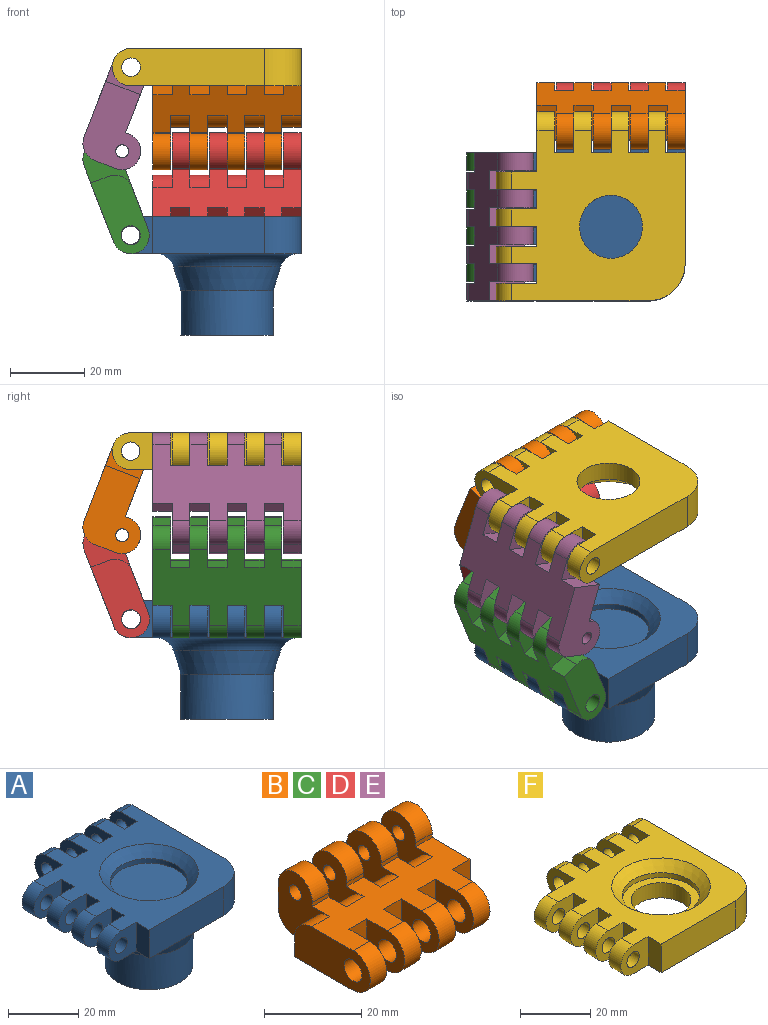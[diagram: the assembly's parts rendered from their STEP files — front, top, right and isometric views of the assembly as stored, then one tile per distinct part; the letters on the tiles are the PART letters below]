
ASSEMBLY  parts=6 mates=4
PART A: 59 faces, bbox 51.8x51.8x32 mm
  f0: cylinder r=8.5mm len=18.12mm, axis (0,0,-1), area 888.1mm2, adj f1,f52,f57
  f1: cylinder r=8.5mm len=17mm, axis (0,0,-1), area 16.5mm2, adj f0,f2
  f2: cylinder r=8.5mm len=17mm, axis (0,0,-1), area 16.5mm2, adj f1,f3
  f3: cylinder r=8.5mm len=17mm, axis (0,0,-1), area 16.5mm2, adj f2,f4
  f4: cylinder r=8.5mm len=17mm, axis (0,0,-1), area 16.5mm2, adj f3,f5
  f5: cylinder r=8.5mm len=7.56mm, axis (0,0,-1), area 1.2mm2, adj f4,f49
  f6: plane 16.2x10mm, normal (0,1,0), area 131.6mm2, adj f14,f15,f18,f38,f47
  f7: plane 11x10mm, normal (0,-1,0), area 79.6mm2, adj f14,f15,f25,f38,f47
  f8: plane 11x10mm, normal (0,1,0), area 79.6mm2, adj f14,f15,f25,f37,f46
  f9: plane 11x10mm, normal (0,-1,0), area 79.6mm2, adj f14,f15,f26,f37,f46
  f10: plane 11x10mm, normal (0,1,0), area 79.6mm2, adj f14,f15,f26,f36,f45
  f11: plane 11x10mm, normal (0,-1,0), area 79.6mm2, adj f14,f15,f27,f36,f45
  f12: plane 11x10mm, normal (0,1,0), area 79.6mm2, adj f14,f15,f27,f35,f44
  f13: plane 11x10mm, normal (0,-1,0), area 79.6mm2, adj f14,f15,f28,f35,f44
  f14: plane 46.83x46mm, normal (0,0,1), area 1209.2mm2, adj f6,f7,f8,f9,f10,f11,f12,f13
  f15: plane 46.83x46mm, normal (0,0,-1), area 664.4mm2, adj f6,f7,f8,f9,f10,f11,f12,f13
  f16: plane 11x10mm, normal (-1,0,0), area 80mm2, adj f14,f15,f24,f32,f40
  f17: plane 11x10mm, normal (1,0,0), area 80mm2, adj f14,f15,f24,f39,f43
  f18: plane 11x10mm, normal (-1,0,0), area 80mm2, adj f6,f14,f15,f39,f43
  f19: plane 41x10mm, normal (1,0,0), area 380mm2, adj f14,f15,f34,f42,f58
  f20: plane 11x10mm, normal (-1,0,0), area 80mm2, adj f14,f15,f30,f34,f42
  f21: plane 11x10mm, normal (1,0,0), area 80mm2, adj f14,f15,f30,f33,f41
  f22: plane 11x10mm, normal (-1,0,0), area 80mm2, adj f14,f15,f31,f33,f41
  f23: plane 11x10mm, normal (1,0,0), area 80mm2, adj f14,f15,f31,f32,f40
  f24: plane 10x5.2mm, normal (0,1,0), area 52mm2, adj f14,f15,f16,f17
  f25: plane 10x5.2mm, normal (-1,0,0), area 52mm2, adj f7,f8,f14,f15
  f26: plane 10x5.2mm, normal (-1,0,0), area 52mm2, adj f9,f10,f14,f15
  f27: plane 10x5.2mm, normal (-1,0,0), area 52mm2, adj f11,f12,f14,f15
  f28: plane 10x5.2mm, normal (-1,0,0), area 52mm2, adj f13,f14,f15,f29
  f29: plane 30x10mm, normal (0,-1,0), area 300mm2, adj f14,f15,f28,f58
  f30: plane 10x5.2mm, normal (0,1,0), area 52mm2, adj f14,f15,f20,f21
  f31: plane 10x5.2mm, normal (0,1,0), area 52mm2, adj f14,f15,f22,f23
  f32: cylinder r=2.5mm len=5mm, axis (-1,0,0), area 75.4mm2, adj f16,f23
  f33: cylinder r=2.5mm len=5mm, axis (-1,0,0), area 75.4mm2, adj f21,f22
  f34: cylinder r=2.5mm len=5mm, axis (-1,0,0), area 75.4mm2, adj f19,f20
  f35: cylinder r=2.5mm len=5mm, axis (0,-1,0), area 75.4mm2, adj f12,f13
  f36: cylinder r=2.5mm len=5mm, axis (0,-1,0), area 75.4mm2, adj f10,f11
  f37: cylinder r=2.5mm len=5mm, axis (0,-1,0), area 75.4mm2, adj f8,f9
  f38: cylinder r=2.5mm len=5mm, axis (0,-1,0), area 75.4mm2, adj f6,f7
  f39: cylinder r=2.5mm len=5mm, axis (-1,0,0), area 75.4mm2, adj f17,f18
  f40: cylinder r=5.08mm len=10mm, axis (-1,0,0), area 67.8mm2, adj f14,f15,f16,f23
  f41: cylinder r=5.08mm len=10mm, axis (-1,0,0), area 67.8mm2, adj f14,f15,f21,f22
  f42: cylinder r=5.08mm len=10mm, axis (-1,0,0), area 67.8mm2, adj f14,f15,f19,f20
  f43: cylinder r=5.08mm len=10mm, axis (-1,0,0), area 67.8mm2, adj f14,f15,f17,f18
  f44: cylinder r=5mm len=10mm, axis (0,-1,0), area 75.4mm2, adj f12,f13,f14,f15
  f45: cylinder r=5mm len=10mm, axis (0,-1,0), area 75.4mm2, adj f10,f11,f14,f15
  f46: cylinder r=5mm len=10mm, axis (0,-1,0), area 75.4mm2, adj f8,f9,f14,f15
  f47: cylinder r=5mm len=10mm, axis (0,-1,0), area 75.4mm2, adj f6,f7,f14,f15
  f48: cylinder r=12.5mm len=25mm, axis (0,0,1), area 942.5mm2, adj f49,f50
  f49: plane 25x25mm, normal (0,0,-1), area 228.2mm2, adj f5,f48,f53
  f50: cone r=12.5mm half-angle=16.7deg, axis (0,0,1), area 568.6mm2, adj f48,f51
  f51: torus R=19.22mm, axis (0,0,1), area 660.5mm2, adj f15,f50
  f52: plane 18.34x18.18mm, normal (0,0,-1), area 35.7mm2, adj f0,f53
  f53: cylinder r=9.7mm len=19.4mm, axis (0,0,1), area 116mm2, adj f49,f52
  f54: plane 22x22mm, normal (0,0,1), area 380.1mm2, adj f55
  f55: cylinder r=11mm len=22mm, axis (0,0,1), area 110.6mm2, adj f54,f56
  f56: cone r=11mm half-angle=45deg, axis (0,0,1), area 333.2mm2, adj f14,f55
  f57: plane 17x17mm, normal (0,0,-1), area 227mm2, adj f0
  f58: cylinder r=10mm len=10mm, axis (0,0,1), area 157.1mm2, adj f14,f15,f19,f29
PART B: 58 faces, bbox 40x32x16 mm
  f0: plane 5.2x5mm, normal (0,1,0), area 26mm2, adj f12,f31,f49,f57
  f1: plane 5.2x5mm, normal (0,1,0), area 26mm2, adj f12,f36,f43,f56
  f2: plane 5.2x5mm, normal (0,1,0), area 26mm2, adj f12,f37,f48,f54
  f3: plane 22x10mm, normal (-1,0,0), area 182.7mm2, adj f11,f12,f13,f22,f26,f55
  f4: plane 11x10mm, normal (1,0,0), area 78mm2, adj f11,f12,f14,f22,f26
  f5: plane 11x10mm, normal (-1,0,0), area 78mm2, adj f11,f12,f14,f21,f25
  f6: plane 11x10mm, normal (1,0,0), area 78mm2, adj f11,f12,f15,f21,f25
  f7: plane 11x10mm, normal (-1,0,0), area 78mm2, adj f11,f12,f15,f20,f24
  f8: plane 11x10mm, normal (1,0,0), area 78mm2, adj f11,f12,f16,f20,f24
  f9: plane 11x10mm, normal (-1,0,0), area 78mm2, adj f11,f12,f16,f19,f23
  f10: plane 11x10mm, normal (1,0,0), area 78mm2, adj f11,f12,f17,f19,f23
  f11: plane 40x17mm, normal (0,0,1), area 451.2mm2, adj f3,f4,f5,f6,f7,f8,f9,f10
  f12: plane 40x22mm, normal (0,0,-1), area 651.2mm2, adj f0,f1,f2,f3,f4,f5,f6,f7
  f13: plane 5.2x5mm, normal (0,1,0), area 26mm2, adj f3,f12,f42,f55
  f14: plane 10x5.2mm, normal (0,-1,0), area 52mm2, adj f4,f5,f11,f12
  f15: plane 10x5.2mm, normal (0,-1,0), area 52mm2, adj f6,f7,f11,f12
  f16: plane 10x5.2mm, normal (0,-1,0), area 52mm2, adj f8,f9,f11,f12
  f17: plane 10x5.2mm, normal (0,-1,0), area 52mm2, adj f10,f11,f12,f18
  f18: plane 21x16mm, normal (1,0,0), area 244.3mm2, adj f11,f12,f17,f27,f28,f29,f30,f53
  f19: cylinder r=5mm len=10mm, axis (1,0,0), area 75.4mm2, adj f9,f10,f11,f12
  f20: cylinder r=5mm len=10mm, axis (1,0,0), area 75.4mm2, adj f7,f8,f11,f12
  f21: cylinder r=5mm len=10mm, axis (1,0,0), area 75.4mm2, adj f5,f6,f11,f12
  f22: cylinder r=5mm len=10mm, axis (1,0,0), area 75.4mm2, adj f3,f4,f11,f12
  f23: cylinder r=2.6mm len=5.2mm, axis (1,0,0), area 78.4mm2, adj f9,f10
  f24: cylinder r=2.6mm len=5.2mm, axis (1,0,0), area 78.4mm2, adj f7,f8
  f25: cylinder r=2.6mm len=5.2mm, axis (1,0,0), area 78.4mm2, adj f5,f6
  f26: cylinder r=2.6mm len=5.2mm, axis (1,0,0), area 78.4mm2, adj f3,f4
  f27: cylinder r=5mm len=5mm, axis (1,0,0), area 37.7mm2, adj f12,f18,f28,f31
  f28: plane 6x4.8mm, normal (0,1,0), area 28.8mm2, adj f18,f27,f29,f31
  f29: cylinder r=5mm len=10mm, axis (1,0,0), area 75.4mm2, adj f18,f28,f30,f31
  f30: plane 4.8x1mm, normal (0,-1,0), area 4.8mm2, adj f11,f18,f29,f31
  f31: plane 16x15mm, normal (-1,0,0), area 139.6mm2, adj f0,f11,f12,f27,f28,f29,f30,f53
  f32: cylinder r=5mm len=10mm, axis (1,0,0), area 75.4mm2, adj f33,f35,f36,f37
  f33: plane 6x4.8mm, normal (0,1,0), area 28.8mm2, adj f32,f34,f36,f37
  f34: cylinder r=5mm len=5mm, axis (1,0,0), area 37.7mm2, adj f12,f33,f36,f37
  f35: plane 4.8x1mm, normal (0,-1,0), area 4.8mm2, adj f11,f32,f36,f37
  f36: plane 16x15mm, normal (-1,0,0), area 139.6mm2, adj f1,f11,f12,f32,f33,f34,f35,f52
  f37: plane 16x15mm, normal (1,0,0), area 139.6mm2, adj f2,f11,f12,f32,f33,f34,f35,f52
  f38: cylinder r=5mm len=10mm, axis (1,0,0), area 75.4mm2, adj f39,f41,f42,f43
  f39: plane 6x4.8mm, normal (0,1,0), area 28.8mm2, adj f38,f40,f42,f43
  f40: cylinder r=5mm len=5mm, axis (1,0,0), area 37.7mm2, adj f12,f39,f42,f43
  f41: plane 4.8x1mm, normal (0,-1,0), area 4.8mm2, adj f11,f38,f42,f43
  f42: plane 16x15mm, normal (-1,0,0), area 139.6mm2, adj f11,f12,f13,f38,f39,f40,f41,f51
  f43: plane 16x15mm, normal (1,0,0), area 139.6mm2, adj f1,f11,f12,f38,f39,f40,f41,f51
  f44: cylinder r=5mm len=10mm, axis (1,0,0), area 75.4mm2, adj f45,f47,f48,f49
  f45: plane 6x4.8mm, normal (0,1,0), area 28.8mm2, adj f44,f46,f48,f49
  f46: cylinder r=5mm len=5mm, axis (1,0,0), area 37.7mm2, adj f12,f45,f48,f49
  f47: plane 4.8x1mm, normal (0,-1,0), area 4.8mm2, adj f11,f44,f48,f49
  f48: plane 16x15mm, normal (-1,0,0), area 139.6mm2, adj f2,f11,f12,f44,f45,f46,f47,f50
  f49: plane 16x15mm, normal (1,0,0), area 139.6mm2, adj f0,f11,f12,f44,f45,f46,f47,f50
  f50: cylinder r=1.75mm len=4.8mm, axis (1,0,0), area 52.8mm2, adj f48,f49
  f51: cylinder r=1.75mm len=4.8mm, axis (1,0,0), area 52.8mm2, adj f42,f43
  f52: cylinder r=1.75mm len=4.8mm, axis (1,0,0), area 52.8mm2, adj f36,f37
  f53: cylinder r=1.75mm len=4.8mm, axis (1,0,0), area 52.8mm2, adj f18,f31
  f54: cylinder r=5mm len=5.2mm, axis (1,0,0), area 40.8mm2, adj f2,f11,f37,f48
  f55: cylinder r=5mm len=5.2mm, axis (1,0,0), area 40.8mm2, adj f3,f11,f13,f42
  f56: cylinder r=5mm len=5.2mm, axis (1,0,0), area 40.8mm2, adj f1,f11,f36,f43
  f57: cylinder r=5mm len=5.2mm, axis (1,0,0), area 40.8mm2, adj f0,f11,f31,f49
PART C: same geometry as B
PART D: same geometry as B
PART E: same geometry as B
PART F: 47 faces, bbox 51x51x10 mm
  f0: cylinder r=8.5mm len=17mm, axis (0,0,1), area 283.1mm2, adj f10,f44
  f1: plane 16.2x10mm, normal (0,1,0), area 131.6mm2, adj f9,f10,f13,f33,f42
  f2: plane 11x10mm, normal (0,-1,0), area 79.6mm2, adj f9,f10,f20,f33,f42
  f3: plane 11x10mm, normal (0,1,0), area 79.6mm2, adj f9,f10,f20,f32,f41
  f4: plane 11x10mm, normal (0,-1,0), area 79.6mm2, adj f9,f10,f21,f32,f41
  f5: plane 11x10mm, normal (0,1,0), area 79.6mm2, adj f9,f10,f21,f31,f40
  f6: plane 11x10mm, normal (0,-1,0), area 79.6mm2, adj f9,f10,f22,f31,f40
  f7: plane 11x10mm, normal (0,1,0), area 79.6mm2, adj f9,f10,f22,f30,f39
  f8: plane 11x10mm, normal (0,-1,0), area 79.6mm2, adj f9,f10,f23,f30,f39
  f9: plane 46.83x46mm, normal (0,0,1), area 1209.2mm2, adj f1,f2,f3,f4,f5,f6,f7,f8
  f10: plane 46.83x46mm, normal (0,0,-1), area 1598mm2, adj f0,f1,f2,f3,f4,f5,f6,f7
  f11: plane 11x10mm, normal (-1,0,0), area 80mm2, adj f9,f10,f19,f27,f35
  f12: plane 11x10mm, normal (1,0,0), area 80mm2, adj f9,f10,f19,f34,f38
  f13: plane 11x10mm, normal (-1,0,0), area 80mm2, adj f1,f9,f10,f34,f38
  f14: plane 41x10mm, normal (1,0,0), area 380mm2, adj f9,f10,f29,f37,f46
  f15: plane 11x10mm, normal (-1,0,0), area 80mm2, adj f9,f10,f25,f29,f37
  f16: plane 11x10mm, normal (1,0,0), area 80mm2, adj f9,f10,f25,f28,f36
  f17: plane 11x10mm, normal (-1,0,0), area 80mm2, adj f9,f10,f26,f28,f36
  f18: plane 11x10mm, normal (1,0,0), area 80mm2, adj f9,f10,f26,f27,f35
  f19: plane 10x5.2mm, normal (0,1,0), area 52mm2, adj f9,f10,f11,f12
  f20: plane 10x5.2mm, normal (-1,0,0), area 52mm2, adj f2,f3,f9,f10
  f21: plane 10x5.2mm, normal (-1,0,0), area 52mm2, adj f4,f5,f9,f10
  f22: plane 10x5.2mm, normal (-1,0,0), area 52mm2, adj f6,f7,f9,f10
  f23: plane 10x5.2mm, normal (-1,0,0), area 52mm2, adj f8,f9,f10,f24
  f24: plane 30x10mm, normal (0,-1,0), area 300mm2, adj f9,f10,f23,f46
  f25: plane 10x5.2mm, normal (0,1,0), area 52mm2, adj f9,f10,f15,f16
  f26: plane 10x5.2mm, normal (0,1,0), area 52mm2, adj f9,f10,f17,f18
  f27: cylinder r=2.5mm len=5mm, axis (-1,0,0), area 75.4mm2, adj f11,f18
  f28: cylinder r=2.5mm len=5mm, axis (-1,0,0), area 75.4mm2, adj f16,f17
  f29: cylinder r=2.5mm len=5mm, axis (-1,0,0), area 75.4mm2, adj f14,f15
  f30: cylinder r=2.5mm len=5mm, axis (0,-1,0), area 75.4mm2, adj f7,f8
  f31: cylinder r=2.5mm len=5mm, axis (0,-1,0), area 75.4mm2, adj f5,f6
  f32: cylinder r=2.5mm len=5mm, axis (0,-1,0), area 75.4mm2, adj f3,f4
  f33: cylinder r=2.5mm len=5mm, axis (0,-1,0), area 75.4mm2, adj f1,f2
  f34: cylinder r=2.5mm len=5mm, axis (-1,0,0), area 75.4mm2, adj f12,f13
  f35: cylinder r=5.08mm len=10mm, axis (-1,0,0), area 67.8mm2, adj f9,f10,f11,f18
  f36: cylinder r=5.08mm len=10mm, axis (-1,0,0), area 67.8mm2, adj f9,f10,f16,f17
  f37: cylinder r=5.08mm len=10mm, axis (-1,0,0), area 67.8mm2, adj f9,f10,f14,f15
  f38: cylinder r=5.08mm len=10mm, axis (-1,0,0), area 67.8mm2, adj f9,f10,f12,f13
  f39: cylinder r=5mm len=10mm, axis (0,-1,0), area 75.4mm2, adj f7,f8,f9,f10
  f40: cylinder r=5mm len=10mm, axis (0,-1,0), area 75.4mm2, adj f5,f6,f9,f10
  f41: cylinder r=5mm len=10mm, axis (0,-1,0), area 75.4mm2, adj f3,f4,f9,f10
  f42: cylinder r=5mm len=10mm, axis (0,-1,0), area 75.4mm2, adj f1,f2,f9,f10
  f43: cylinder r=11mm len=22mm, axis (0,0,1), area 117.5mm2, adj f44,f45
  f44: plane 22x22mm, normal (0,0,1), area 153.2mm2, adj f0,f43
  f45: cone r=11mm half-angle=45deg, axis (0,0,1), area 333.2mm2, adj f9,f43
  f46: cylinder r=10mm len=10mm, axis (0,0,1), area 157.1mm2, adj f9,f10,f14,f24
PLACE A t=(87.3,65.48,29.45)mm fixed
PLACE B rot(axis=(0,0.82,-0.57),180deg) t=(87.3,86.8,105.87)mm
PLACE C rot(axis=(0.49,0.49,0.72),108.7deg) t=(65.98,65.48,8.39)mm
PLACE D rot(axis=(1,0,0),68.7deg) t=(87.3,86.62,8.4)mm
PLACE E rot(axis=(-0.64,0.64,-0.44),133deg) t=(66.16,65.48,105.85)mm
PLACE F rot(axis=(0.71,-0.71,0),180deg) t=(87.3,65.48,84.81)mm
MATE revolute E.f29 <-> C.f29  axis (0,1,0) through (58.99,50.28,57.13)mm
MATE revolute D.f19 <-> A.f32  axis (1,0,0) through (102.1,91.4,34.45)mm
MATE revolute A.f44 <-> C.f19  axis (0,-1,0) through (61.3,50.68,34.45)mm
MATE revolute B.f19 <-> F.f39  axis (-1,0,0) through (102.5,91.48,79.81)mm
